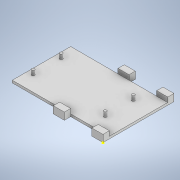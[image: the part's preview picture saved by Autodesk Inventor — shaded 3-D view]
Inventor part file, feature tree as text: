
AUTODESK INVENTOR PART (.ipt)
format: ipt  version: 2021 (Build 250183000, 183)  size: 158,720 bytes
history: native  units: in
note: dims shown in document units (in); Inventor stores cm internally (conversion verified against a paired STEP export)
features: sketch x5, extrude x4
ambient origin geometry x8: Origin, YZ Plane, XZ Plane, XY Plane, X Axis, Y Axis, Z Axis, Center Point
bodies: Solid1 (feature_tree)
feature tree (9):
  extrude  "Extrusion1"  Depth=0.1575in
  extrude  "Extrusion2"  Depth=0.2756in
  sketch  "Sketch3"  dims[d4=0.689in d5=1.4567in]
  extrude  "Extrusion3"  Depth=1.4567in
  extrude  "Extrusion4"  Depth=0.0591in
  sketch  "Sketch1"  dims[d0=0.2756in d1=0.1575in]
  sketch  "Sketch2"  dims[d2=0.7283in d3=0.2756in]
  sketch  "Sketch4"  dims[d6=0.1772in d7=0.0in d8=0.0591in]
  sketch  "Sketch5"  dims[d9=1.4567in d10=0.0in d11=1.2402in d12=1.4567in d13=1.1811in d14=0.0in d15=0.1575in d16=0.0709in d17=0.35in d18=0.0709in d19=1.8in d20=0.1181in d21=0.0in d22=0.35in]
